annotation { "Feature Type Name" : "Feature", "Feature Type Description" : "" }
export const myFeature = defineFeature(function(context is Context, id is Id, definition is map)
    precondition{}
    {
        {
            var Q0;
            Q0=qCreatedBy(makeId("Front.planeOp"),FACE);
            var sketch = newSketch(context, id + "F0", { "sketchPlane" : qUnion([Q0])});
            skLineSegment(sketch, "E0.bottom", {"start": v(0, 0) * mm, "end": v(425, 0) * mm});
            skLineSegment(sketch, "E0.top", {"start": v(0, 380) * mm, "end": v(425, 380) * mm});
            skLineSegment(sketch, "E0.left", {"start": v(0, 0) * mm, "end": v(0, 380) * mm});
            skLineSegment(sketch, "E0.right", {"start": v(425, 0) * mm, "end": v(425, 380) * mm});
            skSolve(sketch);
        }
        {
            var Q0;
            Q0=makeQuery(id+"F0.imprint","IMPRINT",FACE,{"disambiguationData":[TD([[makeQuery(id+"F0.imprint","IMPRINT",EDGE,{"derivedFrom":sQuery(id+"F0.wireOp",EDGE,"E0.bottom")}),1.0]])]});
            extrude(context, id + "F1", {"entities" : qUnion([Q0]), "oppositeDirection" : true, "depth" : 1340 * mm, "offsetDistance" : 25 * mm});
        }
        {
            var Q0;
            Q0=makeQuery(id+"F1.opExtrude","SWEPT_FACE",FACE,{"disambiguationData":[OSD([sQuery(id+"F0.wireOp",EDGE,"E0.bottom")])]});
            var sketch = newSketch(context, id + "F2", { "sketchPlane" : qUnion([Q0])});
            skLineSegment(sketch, "E1", {"start": v(0, 0) * mm, "end": v(425, -1340) * mm, "construction": true});
            skLineSegment(sketch, "E2", {"start": v(425, 0) * mm, "end": v(0, -1340) * mm, "construction": true});
            skLineSegment(sketch, "E3.bottom", {"start": v(437.5, 30) * mm, "end": v(-12.5, 30) * mm});
            skLineSegment(sketch, "E3.top", {"start": v(437.5, -1370) * mm, "end": v(-12.5, -1370) * mm});
            skLineSegment(sketch, "E3.left", {"start": v(437.5, 30) * mm, "end": v(437.5, -1370) * mm});
            skLineSegment(sketch, "E3.right", {"start": v(-12.5, 30) * mm, "end": v(-12.5, -1370) * mm});
            skPoint(sketch, "E3.middle", {"position": v(212.5, -670) * mm});
            skSolve(sketch);
        }
        {
            var Q0;
            Q0=makeQuery(id+"F2.imprint","IMPRINT",FACE,{"disambiguationData":[TD([[makeQuery(id+"F2.imprint","IMPRINT",EDGE,{"derivedFrom":sQuery(id+"F2.wireOp",EDGE,"E3.bottom")}),1.0]])]});
            var Q1;
            {var subQ0=sQuery(id+"F0.wireOp",EDGE,"E0.bottom");Q1=makeQuery(id+"F2.imprint","IMPRINT",FACE,{"disambiguationData":[TD([[makeQuery(id+"F2.imprint","IMPRINT",EDGE,{"derivedFrom":makeQuery(id+"F1.opExtrude","CAP_EDGE",EDGE,{"disambiguationData":[OSD([subQ0])],"isStart":true})}),-1.0]])]});}
            extrude(context, id + "F3", {"entities" : qUnion([Q0, Q1]), "operationType" : NewBodyOperationType.ADD, "depth" : 6 * mm, "offsetDistance" : 25 * mm});
        }
        {
            var Q0;
            Q0=makeQuery(id+"F3.opExtrude","CAP_FACE",FACE,{"disambiguationData":[OSD([sQuery(id+"F2.wireOp",EDGE,"E3.bottom"),sQuery(id+"F2.wireOp",EDGE,"E3.top"),sQuery(id+"F2.wireOp",EDGE,"E3.left"),sQuery(id+"F2.wireOp",EDGE,"E3.right")])],"isStart":true});
            var sketch = newSketch(context, id + "F4", { "sketchPlane" : qUnion([Q0])});
            skLineSegment(sketch, "E4.bottom", {"start": v(-12.5, 1370) * mm, "end": v(437.5, 1370) * mm});
            skLineSegment(sketch, "E4.top", {"start": v(-12.5, -30) * mm, "end": v(437.5, -30) * mm});
            skLineSegment(sketch, "E4.left", {"start": v(-12.5, 1370) * mm, "end": v(-12.5, -30) * mm});
            skLineSegment(sketch, "E4.right", {"start": v(437.5, 1370) * mm, "end": v(437.5, -30) * mm});
            skLineSegment(sketch, "E5.0", {"start": v(-7.5, 1365) * mm, "end": v(432.5, 1365) * mm});
            skLineSegment(sketch, "E5.1", {"start": v(-7.5, 1365) * mm, "end": v(-7.5, -25) * mm});
            skLineSegment(sketch, "E5.2", {"start": v(-7.5, -25) * mm, "end": v(432.5, -25) * mm});
            skLineSegment(sketch, "E5.3", {"start": v(432.5, 1365) * mm, "end": v(432.5, -25) * mm});
            skSolve(sketch);
        }
        {
            var Q0;
            Q0=makeQuery(id+"F4.imprint","IMPRINT",FACE,{"disambiguationData":[TD([[makeQuery(id+"F4.imprint","IMPRINT",EDGE,{"derivedFrom":sQuery(id+"F4.wireOp",EDGE,"E4.bottom")}),1.0]])]});
            extrude(context, id + "F5", {"entities" : qUnion([Q0]), "operationType" : NewBodyOperationType.ADD, "depth" : 50 * mm, "offsetDistance" : 25 * mm});
        }
        {
            var Q0;
            Q0=makeQuery(id+"F0.imprint","IMPRINT",FACE,{"disambiguationData":[TD([[makeQuery(id+"F0.imprint","IMPRINT",EDGE,{"derivedFrom":sQuery(id+"F0.wireOp",EDGE,"E0.bottom")}),1.0]])]});
            var sketch = newSketch(context, id + "F6", { "sketchPlane" : qUnion([Q0])});
            skLineSegment(sketch, "E6.bottom", {"start": v(42.7, 370.54) * mm, "end": v(82.7, 370.54) * mm});
            skLineSegment(sketch, "E6.top", {"start": v(42.7, 200.54) * mm, "end": v(82.7, 200.54) * mm});
            skLineSegment(sketch, "E6.left", {"start": v(42.7, 370.54) * mm, "end": v(42.7, 200.54) * mm});
            skLineSegment(sketch, "E6.right", {"start": v(82.7, 370.54) * mm, "end": v(82.7, 200.54) * mm});
            skSolve(sketch);
        }
        {
            var Q0;
            Q0=qSketchRegion(id+"F6",true);
            extrude(context, id + "F7", {"entities" : qUnion([Q0]), "operationType" : NewBodyOperationType.ADD, "depth" : 30 * mm, "offsetDistance" : 25 * mm});
        }
        {
            var Q0;
            Q0=makeQuery(id+"F1.opExtrude","SWEPT_FACE",FACE,{"disambiguationData":[OSD([sQuery(id+"F0.wireOp",EDGE,"E0.top")])]});
            var sketch = newSketch(context, id + "F8", { "sketchPlane" : qUnion([Q0])});
            skCircle(sketch, "E7", {"center": v(59.42, 86.94) * mm, "radius": 21 * mm});
            skLineSegment(sketch, "E8", {"start": v(59.42, 86.94) * mm, "end": v(59.42, 191.06) * mm});
            skCircle(sketch, "E9", {"center": v(59.42, 191.06) * mm, "radius": 21 * mm});
            skCircle(sketch, "E10", {"center": v(325.1, 88.07) * mm, "radius": 40 * mm});
            skText(sketch, "E11", { "text": "Diesel Oil Tank", "fontName": "OpenSans-Regular.ttf"});
            const initialGuessF8  = {"E11": [0.13776, 1.02845, 0.00311, -1, 0.03459]};
            skSetInitialGuess(sketch, initialGuessF8);
            skSolve(sketch);
        }
        {
            var Q0;
            Q0=makeQuery(id+"F8.imprint","IMPRINT",FACE,{"disambiguationData":[TD([[makeQuery(id+"F8.imprint","IMPRINT",EDGE,{"derivedFrom":sQuery(id+"F8.wireOp",EDGE,"E10")}),1.0]])]});
            extrude(context, id + "F9", {"entities" : qUnion([Q0]), "operationType" : NewBodyOperationType.ADD, "depth" : 60 * mm, "offsetDistance" : 25 * mm});
        }
        {
            var Q0;
            Q0=makeQuery(id+"F8.imprint","IMPRINT",FACE,{"disambiguationData":[TD([[makeQuery(id+"F8.imprint","IMPRINT",EDGE,{"derivedFrom":sQuery(id+"F8.wireOp",EDGE,"E9")}),1.0]])]});
            var Q1;
            Q1=makeQuery(id+"F8.imprint","IMPRINT",FACE,{"disambiguationData":[TD([[makeQuery(id+"F8.imprint","IMPRINT",EDGE,{"derivedFrom":sQuery(id+"F8.wireOp",EDGE,"E7")}),1.0]])]});
            extrude(context, id + "F10", {"entities" : qUnion([Q0, Q1]), "operationType" : NewBodyOperationType.ADD, "depth" : 30 * mm, "offsetDistance" : 25 * mm});
        }
        {
            var Q0;
            Q0=qSketchRegion(id+"F8",true);
            extrude(context, id + "F11", {"entities" : qUnion([Q0]), "operationType" : NewBodyOperationType.ADD, "depth" : 5 * mm, "offsetDistance" : 25 * mm});
        }
        {
            var Q0;
            Q0=makeQuery(id+"F9.opExtrude","CAP_FACE",FACE,{"disambiguationData":[OSD([sQuery(id+"F8.wireOp",EDGE,"E10")])],"isStart":false});
            var sketch = newSketch(context, id + "F12", { "sketchPlane" : qUnion([Q0])});
            skCircle(sketch, "E12", {"center": v(325.1, 88.07) * mm, "radius": 60 * mm});
            skSolve(sketch);
        }
        {
            var Q0;
            Q0=makeQuery(id+"F12.imprint","IMPRINT",FACE,{"disambiguationData":[TD([[makeQuery(id+"F12.imprint","IMPRINT",EDGE,{"derivedFrom":makeQuery(id+"F9.opExtrude","CAP_EDGE",EDGE,{"disambiguationData":[OSD([sQuery(id+"F8.wireOp",EDGE,"E10")])],"isStart":false})}),1.0]])]});
            var Q1;
            Q1=makeQuery(id+"F12.imprint","IMPRINT",FACE,{"disambiguationData":[TD([[makeQuery(id+"F12.imprint","IMPRINT",EDGE,{"derivedFrom":sQuery(id+"F12.wireOp",EDGE,"E12")}),1.0]])]});
            extrude(context, id + "F13", {"entities" : qUnion([Q0, Q1]), "operationType" : NewBodyOperationType.ADD, "depth" : 30 * mm, "offsetDistance" : 25 * mm});
        }
        {
            var Q0;
            Q0=makeQuery(id+"F3.opExtrude","CAP_FACE",FACE,{"disambiguationData":[OSD([sQuery(id+"F2.wireOp",EDGE,"E3.bottom"),sQuery(id+"F2.wireOp",EDGE,"E3.top"),sQuery(id+"F2.wireOp",EDGE,"E3.left"),sQuery(id+"F2.wireOp",EDGE,"E3.right")])],"isStart":false});
            var sketch = newSketch(context, id + "F14", { "sketchPlane" : qUnion([Q0])});
            skLineSegment(sketch, "E13.bottom", {"start": v(437.5, 30) * mm, "end": v(357.5, 30) * mm});
            skLineSegment(sketch, "E13.top", {"start": v(437.5, -50) * mm, "end": v(357.5, -50) * mm});
            skLineSegment(sketch, "E13.left", {"start": v(437.5, 30) * mm, "end": v(437.5, -50) * mm});
            skLineSegment(sketch, "E13.right", {"start": v(357.5, 30) * mm, "end": v(357.5, -50) * mm});
            skLineSegment(sketch, "E14", {"start": v(212.5, -1370) * mm, "end": v(212.5, 191.67) * mm, "construction": true});
            skLineSegment(sketch, "E15", {"start": v(437.5, -670) * mm, "end": v(-92.76, -670) * mm, "construction": true});
            skLineSegment(sketch, "E16.MirrorCS", {"start": v(-12.5, 30) * mm, "end": v(-12.5, -50) * mm});
            skLineSegment(sketch, "E17.MirrorCS", {"start": v(-12.5, 30) * mm, "end": v(67.5, 30) * mm});
            skLineSegment(sketch, "E18.MirrorCS", {"start": v(67.5, 30) * mm, "end": v(67.5, -50) * mm});
            skLineSegment(sketch, "E19.MirrorCS", {"start": v(-12.5, -50) * mm, "end": v(67.5, -50) * mm});
            skLineSegment(sketch, "E20.MirrorCS", {"start": v(437.5, -1370) * mm, "end": v(437.5, -1290) * mm});
            skLineSegment(sketch, "E21.MirrorCS", {"start": v(437.5, -1370) * mm, "end": v(357.5, -1370) * mm});
            skLineSegment(sketch, "E22.MirrorCS", {"start": v(67.5, -1370) * mm, "end": v(67.5, -1290) * mm});
            skLineSegment(sketch, "E23.MirrorCS", {"start": v(437.5, -1290) * mm, "end": v(357.5, -1290) * mm});
            skLineSegment(sketch, "E24.MirrorCS", {"start": v(-12.5, -1370) * mm, "end": v(67.5, -1370) * mm});
            skLineSegment(sketch, "E25.MirrorCS", {"start": v(-12.5, -1370) * mm, "end": v(-12.5, -1290) * mm});
            skLineSegment(sketch, "E26.MirrorCS", {"start": v(357.5, -1370) * mm, "end": v(357.5, -1290) * mm});
            skLineSegment(sketch, "E27.MirrorCS", {"start": v(-12.5, -1290) * mm, "end": v(67.5, -1290) * mm});
            skSolve(sketch);
        }
        {
            var Q0;
            Q0=makeQuery(id+"F14.imprint","IMPRINT",FACE,{"disambiguationData":[TD([[makeQuery(id+"F14.imprint","IMPRINT",EDGE,{"derivedFrom":sQuery(id+"F14.wireOp",EDGE,"E13.bottom")}),1.0]])]});
            var Q1;
            Q1=makeQuery(id+"F14.imprint","IMPRINT",FACE,{"disambiguationData":[TD([[makeQuery(id+"F14.imprint","IMPRINT",EDGE,{"derivedFrom":sQuery(id+"F14.wireOp",EDGE,"E20.MirrorCS")}),-1.0]])]});
            var Q2;
            Q2=makeQuery(id+"F14.imprint","IMPRINT",FACE,{"disambiguationData":[TD([[makeQuery(id+"F14.imprint","IMPRINT",EDGE,{"derivedFrom":sQuery(id+"F14.wireOp",EDGE,"E22.MirrorCS")}),1.0]])]});
            var Q3;
            Q3=makeQuery(id+"F14.imprint","IMPRINT",FACE,{"disambiguationData":[TD([[makeQuery(id+"F14.imprint","IMPRINT",EDGE,{"derivedFrom":sQuery(id+"F14.wireOp",EDGE,"E16.MirrorCS")}),1.0]])]});
            extrude(context, id + "F15", {"entities" : qUnion([Q0, Q1, Q2, Q3]), "operationType" : NewBodyOperationType.ADD, "depth" : 5 * mm, "offsetDistance" : 25 * mm});
        }
        {
            var Q0;
            Q0=makeQuery(id+"F1.opExtrude","SWEPT_FACE",FACE,{"disambiguationData":[OSD([sQuery(id+"F0.wireOp",EDGE,"E0.right")])]});
            var sketch = newSketch(context, id + "F16", { "sketchPlane" : qUnion([Q0])});
            skText(sketch, "E28", { "text": "Diesel Oil Tank", "fontName": "OpenSans-Regular.ttf"});
            const initialGuessF16  = {"E28": [0.34853, 0.1771, 1, 0, 0.07813]};
            skSetInitialGuess(sketch, initialGuessF16);
            skSolve(sketch);
        }
        {
            var Q0;
            Q0 = qSketchRegion(id + "F16", true);
            extrude(context, id + "F17", {"entities" : qUnion([Q0]), "operationType" : NewBodyOperationType.ADD, "depth" : 4 * mm, "offsetDistance" : 25 * mm});
        }
    });